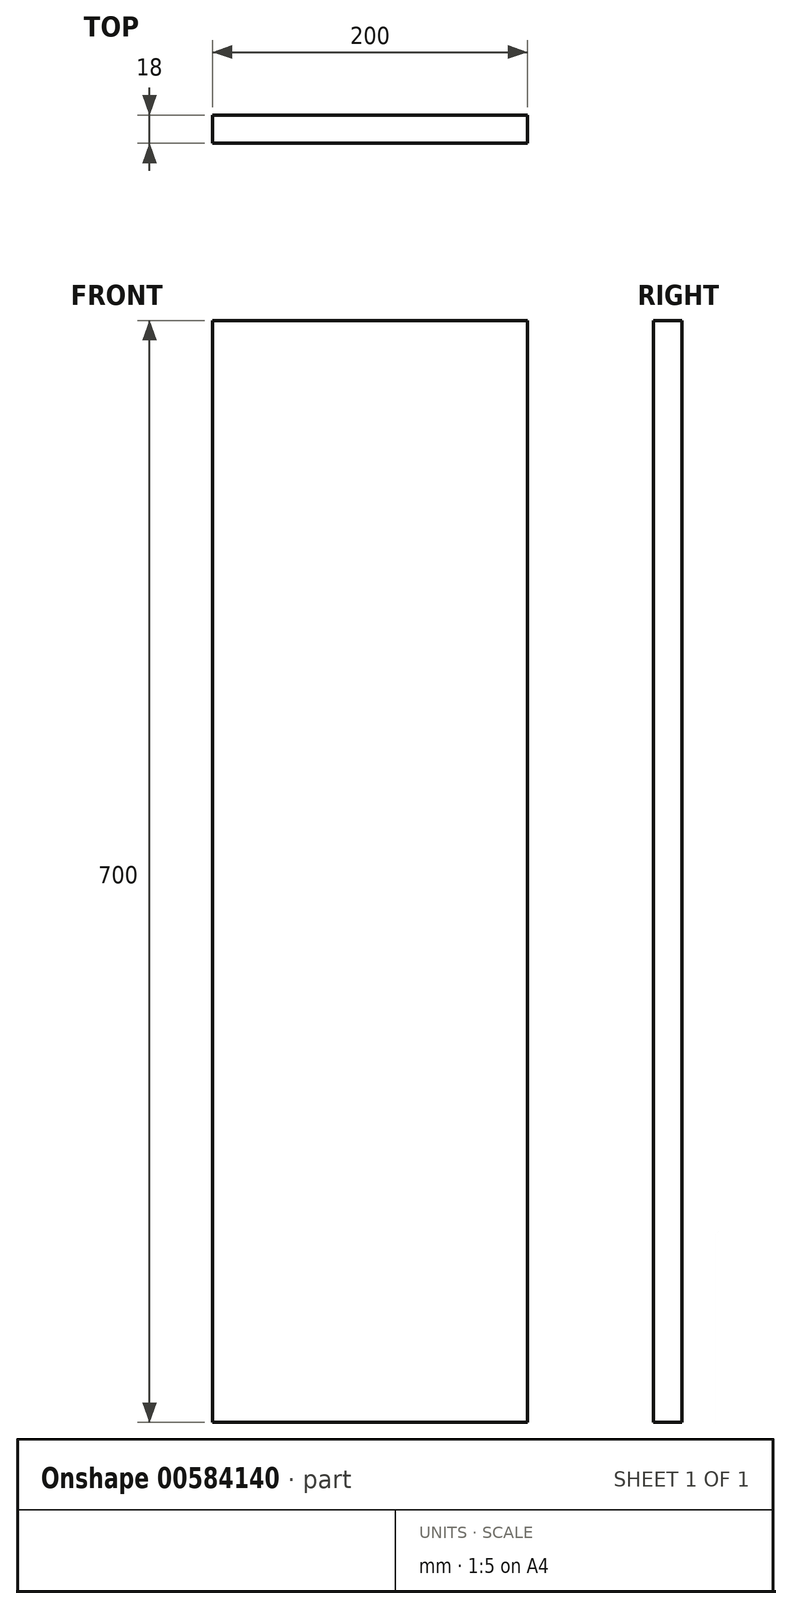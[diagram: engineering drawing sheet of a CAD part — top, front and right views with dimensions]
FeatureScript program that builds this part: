
annotation { "Feature Type Name" : "Feature", "Feature Type Description" : "" }
export const myFeature = defineFeature(function(context is Context, id is Id, definition is map)
    precondition{}
    {
        {
            var Q0;
            Q0=qCreatedBy(makeId("Front.planeOp"),FACE);
            var sketch = newSketch(context, id + "F0", { "sketchPlane" : qUnion([Q0])});
            skLineSegment(sketch, "E0", {"start": v(0, 0) * mm, "end": v(0, -700) * mm});
            skLineSegment(sketch, "E1", {"start": v(0, -700) * mm, "end": v(200, -700) * mm});
            skLineSegment(sketch, "E2", {"start": v(200, -700) * mm, "end": v(200, 0) * mm});
            skLineSegment(sketch, "E3", {"start": v(200, 0) * mm, "end": v(0, 0) * mm});
            skSolve(sketch);
        }
        {
            var Q0;
            Q0 = qSketchRegion(id + "F0", true);
            extrude(context, id + "F1", {"entities" : qUnion([Q0]), "depth" : 18 * mm, "offsetDistance" : 25 * mm});
        }
    });
